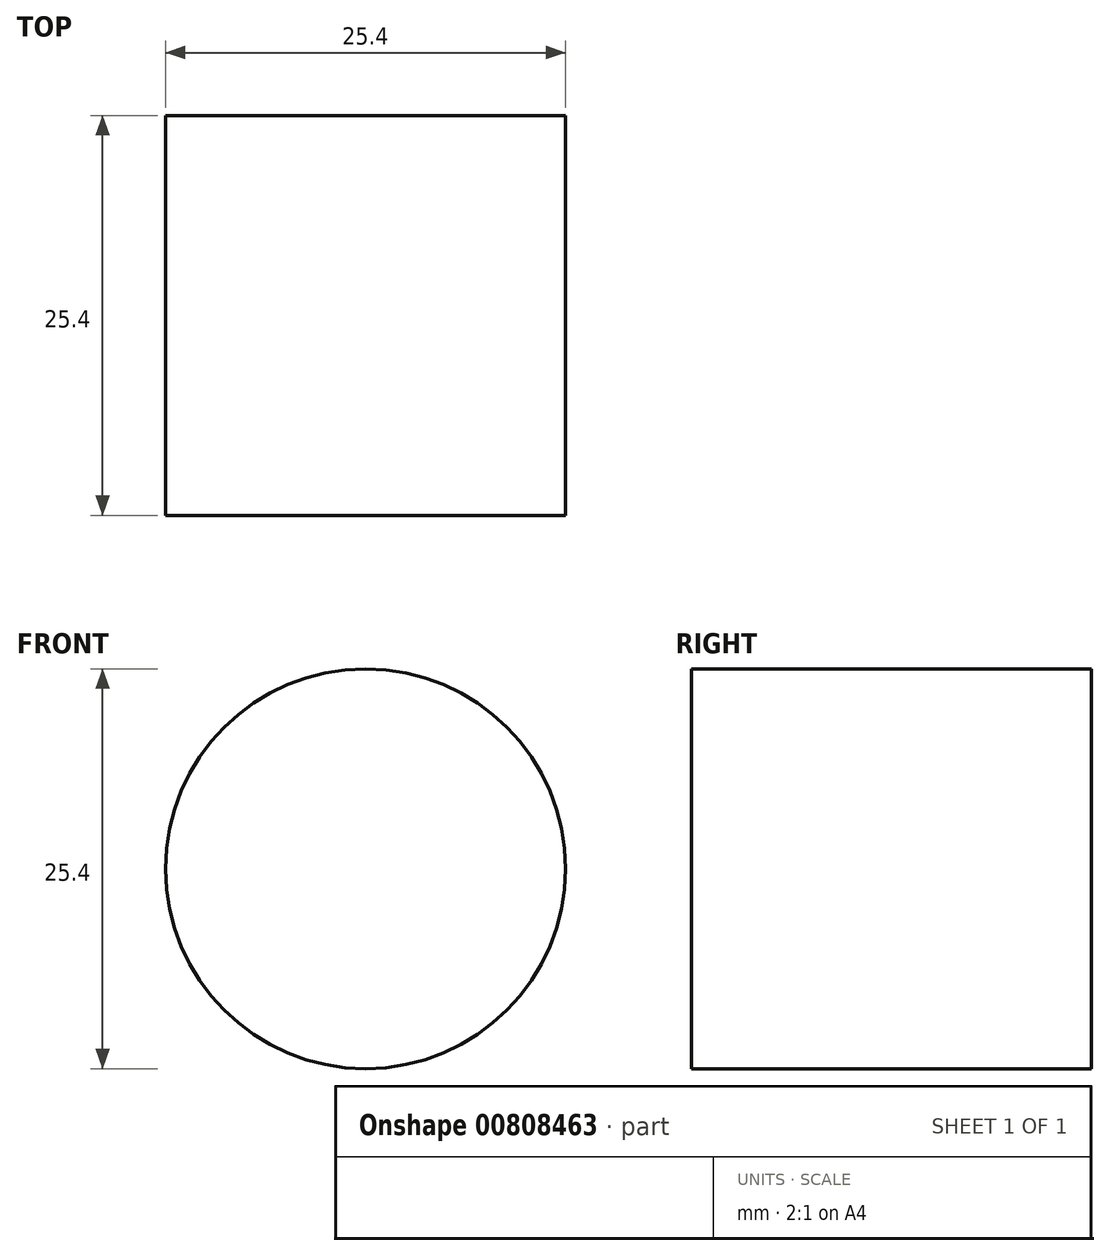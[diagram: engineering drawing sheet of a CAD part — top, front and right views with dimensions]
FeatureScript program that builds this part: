
annotation { "Feature Type Name" : "Feature", "Feature Type Description" : "" }
export const myFeature = defineFeature(function(context is Context, id is Id, definition is map)
    precondition{}
    {
        {
            var Q0;
            Q0=qCreatedBy(makeId("Front.planeOp"),FACE);
            var sketch = newSketch(context, id + "F0", { "sketchPlane" : qUnion([Q0])});
            skCircle(sketch, "E0", {"center": v(0, 0) * mm, "radius": 12.7 * mm});
            skSolve(sketch);
        }
        {
            var Q0;
            Q0 = qSketchRegion(id + "F0", true);
            extrude(context, id + "F1", {"entities" : qUnion([Q0]), "depth" : 25.4 * mm, "offsetDistance" : 25.4 * mm});
        }
    });
